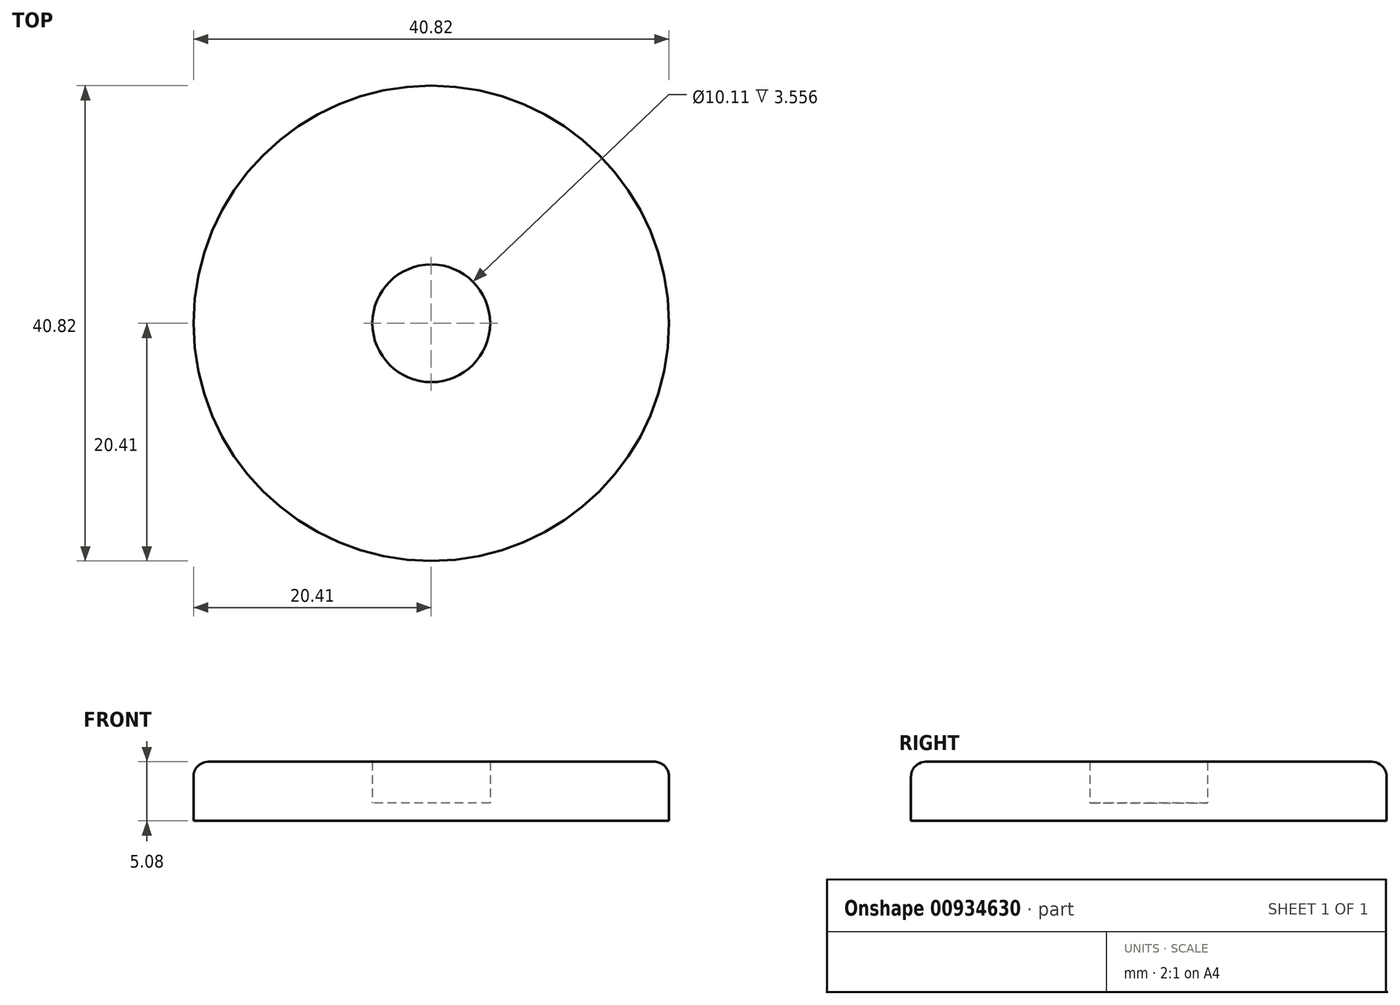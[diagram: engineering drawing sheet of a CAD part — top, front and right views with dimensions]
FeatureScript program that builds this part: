
annotation { "Feature Type Name" : "Feature", "Feature Type Description" : "" }
export const myFeature = defineFeature(function(context is Context, id is Id, definition is map)
    precondition{}
    {
        {
            var Q0;
            Q0=qCreatedBy(makeId("Top.planeOp"),FACE);
            var sketch = newSketch(context, id + "F0", { "sketchPlane" : qUnion([Q0])});
            skCircle(sketch, "E0", {"center": v(0, 0) * mm, "radius": 20.4 * mm});
            skSolve(sketch);
        }
        {
            var Q0;
            Q0=makeQuery(id+"F0.imprint","IMPRINT",FACE,{"disambiguationData":[TD([[makeQuery(id+"F0.imprint","IMPRINT",EDGE,{"derivedFrom":sQuery(id+"F0.wireOp",EDGE,"E0")}),1.0]])]});
            var sketch = newSketch(context, id + "F1", { "sketchPlane" : qUnion([Q0])});
            skCircle(sketch, "E1", {"center": v(0, 0) * mm, "radius": 5.05 * mm});
            skSolve(sketch);
        }
        {
            var Q0;
            Q0=makeQuery(id+"F1.imprint","IMPRINT",FACE,{"disambiguationData":[TD([[makeQuery(id+"F1.imprint","IMPRINT",EDGE,{"derivedFrom":sQuery(id+"F1.wireOp",EDGE,"E1")}),-1.0]])]});
            extrude(context, id + "F2", {"entities" : qUnion([Q0]), "depth" : 5.08 * mm, "offsetDistance" : 25.4 * mm});
        }
        {
            var Q0;
            Q0=qCreatedBy(makeId("Top.planeOp"),FACE);
            var sketch = newSketch(context, id + "F3", { "sketchPlane" : qUnion([Q0])});
            skCircle(sketch, "E2", {"center": v(0, 0) * mm, "radius": 9.38 * mm});
            skSolve(sketch);
        }
        {
            var Q0;
            Q0=qSketchRegion(id+"F3",true);
            var Q1;
            Q1=qSketchRegion(id+"FGiIpizp7XEVMoY_0",true);
            extrude(context, id + "F4", {"entities" : qUnion([Q0, Q1]), "operationType" : NewBodyOperationType.ADD, "depth" : 1.52 * mm, "offsetDistance" : 25.4 * mm});
        }
        {
            var Q0;
            Q0=makeQuery(id+"F2.opExtrude","CAP_FACE",FACE,{"disambiguationData":[OSD([sQuery(id+"F0.wireOp",EDGE,"E0"),sQuery(id+"F1.wireOp",EDGE,"E1")])],"isStart":false});
            var sketch = newSketch(context, id + "F5", { "sketchPlane" : qUnion([Q0])});
            skText(sketch, "E3", { "text": "Raymond\n\n  Strange\n", "fontName": "OpenSans-Bold.ttf"});
            const initialGuessF5  = {"E3": [-0.01558, 0.00673, 1, 0, 0.00476]};
            skSetInitialGuess(sketch, initialGuessF5);
            skSolve(sketch);
        }
        {
            var Q0;
            Q0=makeQuery(id+"F2.opExtrude","CAP_EDGE",EDGE,{"disambiguationData":[OSD([sQuery(id+"F0.wireOp",EDGE,"E0")])],"isStart":false});
            fillet(context, id + "F6", {"entities" : qUnion([Q0]), "radius" : 1.27 * mm, "tangentPropagation" : true, "allowEdgeOverflow" : false});
        }
    });
